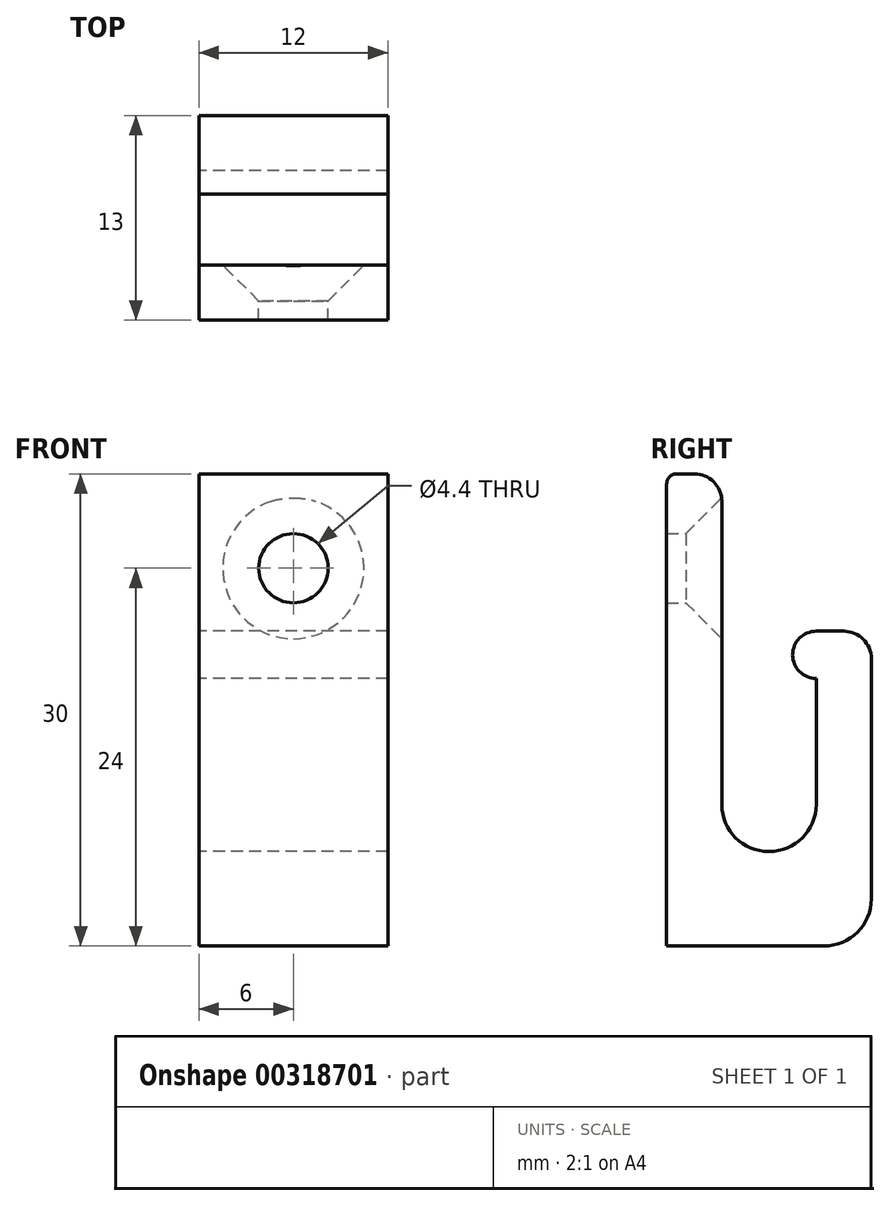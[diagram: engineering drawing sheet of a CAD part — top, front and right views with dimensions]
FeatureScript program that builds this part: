
annotation { "Feature Type Name" : "Feature", "Feature Type Description" : "" }
export const myFeature = defineFeature(function(context is Context, id is Id, definition is map)
    precondition{}
    {
        {
            var Q0;
            Q0=qCreatedBy(makeId("Right.planeOp"),FACE);
            var sketch = newSketch(context, id + "F0", { "sketchPlane" : qUnion([Q0])});
            skLineSegment(sketch, "E0", {"start": v(0, 0) * mm, "end": v(0, 29.35) * mm});
            skLineSegment(sketch, "E1", {"start": v(0.65, 30) * mm, "end": v(1.75, 30) * mm});
            skLineSegment(sketch, "E2", {"start": v(3.5, 28.25) * mm, "end": v(3.5, 9) * mm});
            skLineSegment(sketch, "E3", {"start": v(6.5, 6) * mm, "end": v(6.5, 6) * mm});
            skLineSegment(sketch, "E4", {"start": v(9.5, 9) * mm, "end": v(9.5, 20) * mm});
            skLineSegment(sketch, "E5", {"start": v(9.5, 20) * mm, "end": v(11.25, 20) * mm});
            skLineSegment(sketch, "E6", {"start": v(13, 18.25) * mm, "end": v(13, 3) * mm});
            skLineSegment(sketch, "E7", {"start": v(10, 0) * mm, "end": v(0, 0) * mm});
            skCircle(sketch, "E8", {"center": v(9.5, 18.5) * mm, "radius": 1.5 * mm});
            skPoint(sketch, "E9.visualSharp", {"position": v(3.5, 6) * mm});
            skArc(sketch, "E9.filletArc", {"start": v(3.5, 9) * mm, "mid": v(4.38, 6.88) * mm, "end": v(6.5, 6) * mm});
            skPoint(sketch, "E10.visualSharp", {"position": v(9.5, 6) * mm});
            skArc(sketch, "E10.filletArc", {"start": v(6.5, 6) * mm, "mid": v(8.62, 6.88) * mm, "end": v(9.5, 9) * mm});
            skPoint(sketch, "E11.visualSharp", {"position": v(13, 20) * mm});
            skArc(sketch, "E11.filletArc", {"start": v(13, 18.25) * mm, "mid": v(12.49, 19.49) * mm, "end": v(11.25, 20) * mm});
            skPoint(sketch, "E12.visualSharp", {"position": v(13, 0) * mm});
            skArc(sketch, "E12.filletArc", {"start": v(10, 0) * mm, "mid": v(12.12, 0.88) * mm, "end": v(13, 3) * mm});
            skPoint(sketch, "E13.visualSharp", {"position": v(3.5, 30) * mm});
            skArc(sketch, "E13.filletArc", {"start": v(3.5, 28.25) * mm, "mid": v(2.99, 29.49) * mm, "end": v(1.75, 30) * mm});
            skPoint(sketch, "E14.visualSharp", {"position": v(0, 30) * mm});
            skArc(sketch, "E14.filletArc", {"start": v(0.65, 30) * mm, "mid": v(0.19, 29.81) * mm, "end": v(0, 29.35) * mm});
            skSolve(sketch);
        }
        {
            var Q0;
            Q0 = qSketchRegion(id + "F0", true);
            extrude(context, id + "F1", {"entities" : qUnion([Q0]), "endBound" : BoundingType.SYMMETRIC, "depth" : 12 * mm});
        }
        {
            var Q0;
            Q0=makeQuery(id+"F1.opExtrude","SWEPT_FACE",FACE,{"disambiguationData":[OSD([sQuery(id+"F0.wireOp",EDGE,"E2")])]});
            var sketch = newSketch(context, id + "F2", { "sketchPlane" : qUnion([Q0])});
            skPoint(sketch, "E15", {"position": v(0, 24) * mm});
            skCircle(sketch, "E16", {"center": v(0, 24) * mm, "radius": 2 * mm});
            skSolve(sketch);
        }
        {
            var Q0;
            Q0 = qSketchRegion(id + "F2", true);
            extrude(context, id + "F3", {"entities" : qUnion([Q0]), "operationType" : NewBodyOperationType.REMOVE, "oppositeDirection" : true, "depth" : 25 * mm});
        }
        {
            var Q0;
            Q0=sQuery(id+"F2.wireOp",VERTEX,"E15");
            var Q1;
            Q1=makeQuery(id+"F1.opExtrude","SWEPT_BODY",BODY,{"disambiguationData":[OSD([sQuery(id+"F0.wireOp",EDGE,"E0"),sQuery(id+"F0.wireOp",EDGE,"E1"),sQuery(id+"F0.wireOp",EDGE,"E2"),sQuery(id+"F0.wireOp",EDGE,"E4"),sQuery(id+"F0.wireOp",EDGE,"E5"),sQuery(id+"F0.wireOp",EDGE,"E6"),sQuery(id+"F0.wireOp",EDGE,"E7"),sQuery(id+"F0.wireOp",EDGE,"E8"),sQuery(id+"F0.wireOp",EDGE,"E9.filletArc"),sQuery(id+"F0.wireOp",EDGE,"E10.filletArc"),sQuery(id+"F0.wireOp",EDGE,"E11.filletArc"),sQuery(id+"F0.wireOp",EDGE,"E12.filletArc"),sQuery(id+"F0.wireOp",EDGE,"E13.filletArc"),sQuery(id+"F0.wireOp",EDGE,"E14.filletArc")])]});
            hole(context, id + "F4", {"style" : HoleStyle.C_SINK, "endStyle" : HoleEndStyle.THROUGH, "standardTappedOrClearance" : lookupTablePath({ "standard" : "ISO", "fit" : "Normal", "size" : "M4", "type" : "Clearance" }), "standardBlindInLast" : lookupTablePath({ "fit" : "Standard", "standard" : "ISO", "size" : "M4", "type" : "Clearance" }), "holeDiameter" : 4.4 * mm, "cSinkDiameter" : 8.96 * mm, "cSinkAngle" : 90 * degree, "tappedDepth" : 12 * mm, "tapClearance" : 3, "startFromSketch" : true, "locations" : qUnion([Q0]), "scope" : qUnion([Q1])});
        }
    });
